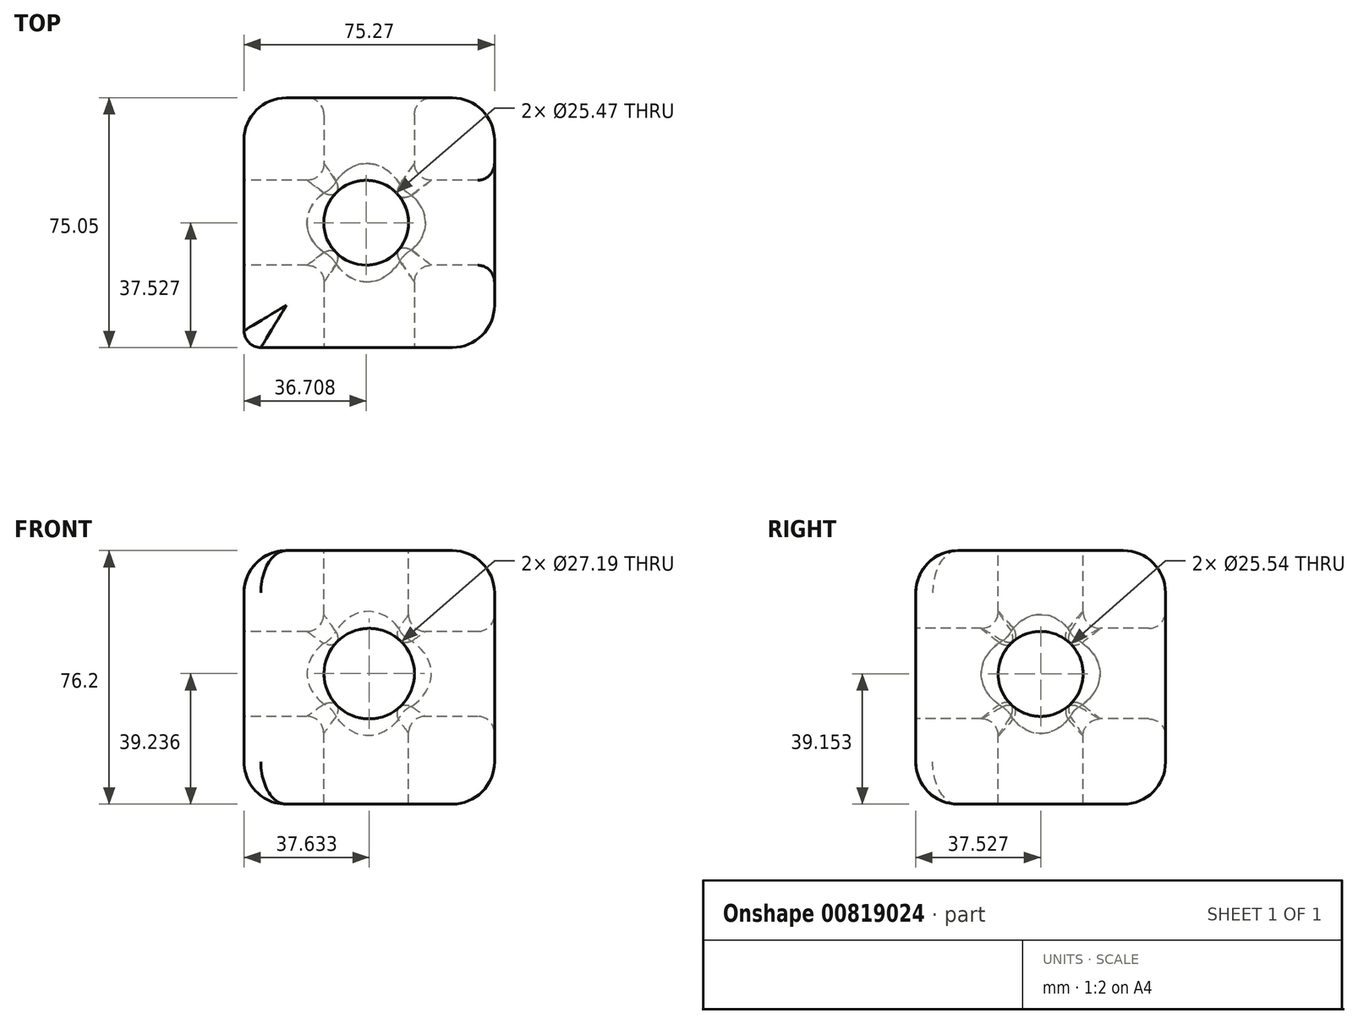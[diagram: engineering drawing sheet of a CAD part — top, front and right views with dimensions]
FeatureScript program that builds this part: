
annotation { "Feature Type Name" : "Feature", "Feature Type Description" : "" }
export const myFeature = defineFeature(function(context is Context, id is Id, definition is map)
    precondition{}
    {
        {
            var Q0;
            Q0=qCreatedBy(makeId("Top.planeOp"),FACE);
            var sketch = newSketch(context, id + "F0", { "sketchPlane" : qUnion([Q0])});
            skLineSegment(sketch, "E0.bottom", {"start": v(0, 0) * mm, "end": v(-75.27, 0) * mm});
            skLineSegment(sketch, "E0.top", {"start": v(0, -75.05) * mm, "end": v(-75.27, -75.05) * mm});
            skLineSegment(sketch, "E0.left", {"start": v(0, 0) * mm, "end": v(0, -75.05) * mm});
            skLineSegment(sketch, "E0.right", {"start": v(-75.27, 0) * mm, "end": v(-75.27, -75.05) * mm});
            skSolve(sketch);
        }
        {
            var Q0;
            Q0=makeQuery(id+"F0.imprint","IMPRINT",FACE,{"disambiguationData":[TD([[makeQuery(id+"F0.imprint","IMPRINT",EDGE,{"derivedFrom":sQuery(id+"F0.wireOp",EDGE,"E0.bottom")}),1.0]])]});
            extrude(context, id + "F1", {"entities" : qUnion([Q0]), "depth" : 76.2 * mm, "offsetDistance" : 25.4 * mm});
        }
        {
            var Q0;
            Q0=makeQuery(id+"F1.opExtrude","SWEPT_FACE",FACE,{"disambiguationData":[OSD([sQuery(id+"F0.wireOp",EDGE,"E0.top")])]});
            var sketch = newSketch(context, id + "F2", { "sketchPlane" : qUnion([Q0])});
            skCircle(sketch, "E1", {"center": v(-37.64, 39.24) * mm, "radius": 13.6 * mm});
            skPoint(sketch, "E1.centerSnap0", {"position": v(-37.64, 0) * mm});
            skSolve(sketch);
        }
        {
            var Q0;
            Q0=makeQuery(id+"F2.imprint","IMPRINT",FACE,{"disambiguationData":[TD([[makeQuery(id+"F2.imprint","IMPRINT",EDGE,{"derivedFrom":sQuery(id+"F2.wireOp",EDGE,"E1")}),1.0]])]});
            var Q1;
            Q1=sQuery(id+"F2.wireOp",EDGE,"E1");
            extrude(context, id + "F3", {"entities" : qUnion([Q0]), "operationType" : NewBodyOperationType.REMOVE, "surfaceEntities" : qUnion([Q1]), "oppositeDirection" : true, "depth" : 76.2 * mm, "offsetDistance" : 25.4 * mm});
        }
        {
            var Q0;
            Q0=makeQuery(id+"F1.opExtrude","SWEPT_FACE",FACE,{"disambiguationData":[OSD([sQuery(id+"F0.wireOp",EDGE,"E0.right")])]});
            var sketch = newSketch(context, id + "F4", { "sketchPlane" : qUnion([Q0])});
            skCircle(sketch, "E2", {"center": v(37.52, 39.15) * mm, "radius": 12.77 * mm});
            skPoint(sketch, "E2.centerSnap0", {"position": v(37.52, 0) * mm});
            skSolve(sketch);
        }
        {
            var Q0;
            Q0=makeQuery(id+"F4.imprint","IMPRINT",FACE,{"disambiguationData":[TD([[makeQuery(id+"F4.imprint","IMPRINT",EDGE,{"derivedFrom":sQuery(id+"F4.wireOp",EDGE,"E2")}),1.0]])]});
            extrude(context, id + "F5", {"entities" : qUnion([Q0]), "operationType" : NewBodyOperationType.REMOVE, "oppositeDirection" : true, "depth" : 76.2 * mm, "offsetDistance" : 25.4 * mm});
        }
        {
            var Q0;
            Q0=makeQuery(id+"F1.opExtrude","CAP_FACE",FACE,{"disambiguationData":[OSD([sQuery(id+"F0.wireOp",EDGE,"E0.bottom"),sQuery(id+"F0.wireOp",EDGE,"E0.top"),sQuery(id+"F0.wireOp",EDGE,"E0.left"),sQuery(id+"F0.wireOp",EDGE,"E0.right")])],"isStart":false});
            var sketch = newSketch(context, id + "F6", { "sketchPlane" : qUnion([Q0])});
            skCircle(sketch, "E3", {"center": v(-38.56, -37.52) * mm, "radius": 12.73 * mm});
            skPoint(sketch, "E3.centerSnap0", {"position": v(0, -37.52) * mm});
            skSolve(sketch);
        }
        {
            var Q0;
            Q0=makeQuery(id+"F6.imprint","IMPRINT",FACE,{"disambiguationData":[TD([[makeQuery(id+"F6.imprint","IMPRINT",EDGE,{"derivedFrom":sQuery(id+"F6.wireOp",EDGE,"E3")}),1.0]])]});
            var Q1;
            Q1=sQuery(id+"F6.wireOp",EDGE,"E3");
            extrude(context, id + "F7", {"entities" : qUnion([Q0]), "operationType" : NewBodyOperationType.REMOVE, "surfaceEntities" : qUnion([Q1]), "oppositeDirection" : true, "depth" : 76.2 * mm, "offsetDistance" : 25.4 * mm});
        }
        {
            var Q0;
            Q0=makeQuery(id+"F1.opExtrude","CAP_EDGE",EDGE,{"disambiguationData":[OSD([sQuery(id+"F0.wireOp",EDGE,"E0.top")])],"isStart":false});
            var Q1;
            Q1=makeQuery(id+"F1.opExtrude","CAP_EDGE",EDGE,{"disambiguationData":[OSD([sQuery(id+"F0.wireOp",EDGE,"E0.right")])],"isStart":false});
            var Q2;
            Q2=makeQuery(id+"F1.opExtrude","CAP_EDGE",EDGE,{"disambiguationData":[OSD([sQuery(id+"F0.wireOp",EDGE,"E0.bottom")])],"isStart":false});
            var Q3;
            Q3=makeQuery(id+"F1.opExtrude","CAP_EDGE",EDGE,{"disambiguationData":[OSD([sQuery(id+"F0.wireOp",EDGE,"E0.left")])],"isStart":false});
            var Q4;
            Q4=makeQuery(id+"F1.opExtrude","SWEPT_EDGE",EDGE,{"disambiguationData":[OSD([sQuery(id+"F0.wireOp",EDGE,"E0.top"),sQuery(id+"F0.wireOp",EDGE,"E0.left")])]});
            var Q5;
            Q5=makeQuery(id+"F1.opExtrude","CAP_EDGE",EDGE,{"disambiguationData":[OSD([sQuery(id+"F0.wireOp",EDGE,"E0.top")])],"isStart":true});
            var Q6;
            Q6=makeQuery(id+"F1.opExtrude","CAP_EDGE",EDGE,{"disambiguationData":[OSD([sQuery(id+"F0.wireOp",EDGE,"E0.left")])],"isStart":true});
            var Q7;
            Q7=makeQuery(id+"F1.opExtrude","CAP_EDGE",EDGE,{"disambiguationData":[OSD([sQuery(id+"F0.wireOp",EDGE,"E0.right")])],"isStart":true});
            var Q8;
            Q8=makeQuery(id+"F1.opExtrude","SWEPT_EDGE",EDGE,{"disambiguationData":[OSD([sQuery(id+"F0.wireOp",EDGE,"E0.bottom"),sQuery(id+"F0.wireOp",EDGE,"E0.right")])]});
            var Q9;
            Q9=makeQuery(id+"F1.opExtrude","CAP_EDGE",EDGE,{"disambiguationData":[OSD([sQuery(id+"F0.wireOp",EDGE,"E0.bottom")])],"isStart":true});
            var Q10;
            Q10=makeQuery(id+"F1.opExtrude","SWEPT_EDGE",EDGE,{"disambiguationData":[OSD([sQuery(id+"F0.wireOp",EDGE,"E0.bottom"),sQuery(id+"F0.wireOp",EDGE,"E0.left")])]});
            fillet(context, id + "F8", {"entities" : qUnion([Q0, Q1, Q2, Q3, Q4, Q5, Q6, Q7, Q8, Q9, Q10]), "radius" : 12.7 * mm, "tangentPropagation" : true, "allowEdgeOverflow" : false});
        }
        {
            var Q0;
            Q0=makeQuery(id+"F5.boolean.opBoolean","COPY",EDGE,{"derivedFrom":makeQuery(id+"F5.opExtrude","CAP_EDGE",EDGE,{"disambiguationData":[OSD([sQuery(id+"F4.wireOp",EDGE,"E2")])],"isStart":true})});
            var Q1;
            Q1=makeQuery(id+"F1.opExtrude","SWEPT_EDGE",EDGE,{"disambiguationData":[OSD([sQuery(id+"F0.wireOp",EDGE,"E0.top"),sQuery(id+"F0.wireOp",EDGE,"E0.right")])]});
            var Q2;
            Q2=makeQuery(id+"F3.boolean.opBoolean","COPY",EDGE,{"derivedFrom":makeQuery(id+"F3.opExtrude","CAP_EDGE",EDGE,{"disambiguationData":[OSD([sQuery(id+"F2.wireOp",EDGE,"E1")])],"isStart":true})});
            var Q3;
            Q3=makeQuery(id+"F7.boolean.opBoolean","COPY",EDGE,{"derivedFrom":makeQuery(id+"F7.opExtrude","CAP_EDGE",EDGE,{"disambiguationData":[OSD([sQuery(id+"F6.wireOp",EDGE,"E3")])],"isStart":true})});
            var Q4;
            Q4=makeQuery(id+"F5.boolean.opBoolean","INTERSECT",EDGE,{"derivedFrom":[makeQuery(id+"F1.opExtrude","SWEPT_FACE",FACE,{"disambiguationData":[OSD([sQuery(id+"F0.wireOp",EDGE,"E0.left")])]}),makeQuery(id+"F5.opExtrude","SWEPT_FACE",FACE,{"disambiguationData":[OSD([sQuery(id+"F4.wireOp",EDGE,"E2")])]})]});
            var Q5;
            Q5=makeQuery(id+"F7.boolean.opBoolean","COPY",EDGE,{"derivedFrom":makeQuery(id+"F7.opExtrude","CAP_EDGE",EDGE,{"disambiguationData":[OSD([sQuery(id+"F6.wireOp",EDGE,"E3")])],"isStart":false})});
            var Q6;
            Q6=makeQuery(id+"F3.boolean.opBoolean","INTERSECT",EDGE,{"derivedFrom":[makeQuery(id+"F1.opExtrude","SWEPT_FACE",FACE,{"disambiguationData":[OSD([sQuery(id+"F0.wireOp",EDGE,"E0.bottom")])]}),makeQuery(id+"F3.opExtrude","SWEPT_FACE",FACE,{"disambiguationData":[OSD([sQuery(id+"F2.wireOp",EDGE,"E1")])]})]});
            fillet(context, id + "F9", {"entities" : qUnion([Q0, Q1, Q2, Q3, Q4, Q5, Q6]), "radius" : 5.08 * mm, "tangentPropagation" : true, "allowEdgeOverflow" : false});
        }
        {
            var Q0;
            Q0=makeQuery(id+"F7.boolean.opBoolean","SPLIT",EDGE,{"disambiguationData":[OD(1.0)],"derivedFrom":makeQuery(id+"F5.boolean.opBoolean","INTERSECT",EDGE,{"disambiguationData":[OD(1.0)],"derivedFrom":[makeQuery(id+"F3.boolean.opBoolean","COPY",FACE,{"derivedFrom":makeQuery(id+"F3.opExtrude","SWEPT_FACE",FACE,{"disambiguationData":[OSD([sQuery(id+"F2.wireOp",EDGE,"E1")])]})}),makeQuery(id+"F5.opExtrude","SWEPT_FACE",FACE,{"disambiguationData":[OSD([sQuery(id+"F4.wireOp",EDGE,"E2")])]})]})});
            var Q1;
            Q1=makeQuery(id+"F7.boolean.opBoolean","SPLIT",EDGE,{"disambiguationData":[OD(0.0)],"derivedFrom":makeQuery(id+"F5.boolean.opBoolean","INTERSECT",EDGE,{"disambiguationData":[OD(1.0)],"derivedFrom":[makeQuery(id+"F3.boolean.opBoolean","COPY",FACE,{"derivedFrom":makeQuery(id+"F3.opExtrude","SWEPT_FACE",FACE,{"disambiguationData":[OSD([sQuery(id+"F2.wireOp",EDGE,"E1")])]})}),makeQuery(id+"F5.opExtrude","SWEPT_FACE",FACE,{"disambiguationData":[OSD([sQuery(id+"F4.wireOp",EDGE,"E2")])]})]})});
            var Q2;
            Q2=makeQuery(id+"F7.boolean.opBoolean","INTERSECT",EDGE,{"disambiguationData":[OD(1.0)],"derivedFrom":[makeQuery(id+"F5.boolean.opBoolean","COPY",FACE,{"disambiguationData":[TD([makeQuery(id+"F1.opExtrude","SWEPT_FACE",FACE,{"disambiguationData":[OSD([sQuery(id+"F0.wireOp",EDGE,"E0.left")])]})])],"derivedFrom":makeQuery(id+"F5.opExtrude","SWEPT_FACE",FACE,{"disambiguationData":[OSD([sQuery(id+"F4.wireOp",EDGE,"E2")])]})}),makeQuery(id+"F7.opExtrude","SWEPT_FACE",FACE,{"disambiguationData":[OSD([sQuery(id+"F6.wireOp",EDGE,"E3")])]})]});
            var Q3;
            Q3=makeQuery(id+"F7.boolean.opBoolean","INTERSECT",EDGE,{"disambiguationData":[OD(0.0)],"derivedFrom":[makeQuery(id+"F5.boolean.opBoolean","COPY",FACE,{"disambiguationData":[TD([makeQuery(id+"F1.opExtrude","SWEPT_FACE",FACE,{"disambiguationData":[OSD([sQuery(id+"F0.wireOp",EDGE,"E0.left")])]})])],"derivedFrom":makeQuery(id+"F5.opExtrude","SWEPT_FACE",FACE,{"disambiguationData":[OSD([sQuery(id+"F4.wireOp",EDGE,"E2")])]})}),makeQuery(id+"F7.opExtrude","SWEPT_FACE",FACE,{"disambiguationData":[OSD([sQuery(id+"F6.wireOp",EDGE,"E3")])]})]});
            var Q4;
            Q4=makeQuery(id+"F7.boolean.opBoolean","INTERSECT",EDGE,{"disambiguationData":[OD(0.0)],"derivedFrom":[makeQuery(id+"F3.boolean.opBoolean","COPY",FACE,{"derivedFrom":makeQuery(id+"F3.opExtrude","SWEPT_FACE",FACE,{"disambiguationData":[OSD([sQuery(id+"F2.wireOp",EDGE,"E1")])]})}),makeQuery(id+"F7.opExtrude","SWEPT_FACE",FACE,{"disambiguationData":[OSD([sQuery(id+"F6.wireOp",EDGE,"E3")])]})]});
            var Q5;
            Q5=makeQuery(id+"F7.boolean.opBoolean","SPLIT",EDGE,{"disambiguationData":[OD(0.0)],"derivedFrom":makeQuery(id+"F5.boolean.opBoolean","INTERSECT",EDGE,{"disambiguationData":[OD(0.0)],"derivedFrom":[makeQuery(id+"F3.boolean.opBoolean","COPY",FACE,{"derivedFrom":makeQuery(id+"F3.opExtrude","SWEPT_FACE",FACE,{"disambiguationData":[OSD([sQuery(id+"F2.wireOp",EDGE,"E1")])]})}),makeQuery(id+"F5.opExtrude","SWEPT_FACE",FACE,{"disambiguationData":[OSD([sQuery(id+"F4.wireOp",EDGE,"E2")])]})]})});
            var Q6;
            Q6=makeQuery(id+"F7.boolean.opBoolean","INTERSECT",EDGE,{"disambiguationData":[OD(0.0)],"derivedFrom":[makeQuery(id+"F5.boolean.opBoolean","COPY",FACE,{"disambiguationData":[TD([makeQuery(id+"F1.opExtrude","SWEPT_FACE",FACE,{"disambiguationData":[OSD([sQuery(id+"F0.wireOp",EDGE,"E0.right")])]})])],"derivedFrom":makeQuery(id+"F5.opExtrude","SWEPT_FACE",FACE,{"disambiguationData":[OSD([sQuery(id+"F4.wireOp",EDGE,"E2")])]})}),makeQuery(id+"F7.opExtrude","SWEPT_FACE",FACE,{"disambiguationData":[OSD([sQuery(id+"F6.wireOp",EDGE,"E3")])]})]});
            var Q7;
            Q7=makeQuery(id+"F7.boolean.opBoolean","INTERSECT",EDGE,{"disambiguationData":[OD(3.0)],"derivedFrom":[makeQuery(id+"F3.boolean.opBoolean","COPY",FACE,{"derivedFrom":makeQuery(id+"F3.opExtrude","SWEPT_FACE",FACE,{"disambiguationData":[OSD([sQuery(id+"F2.wireOp",EDGE,"E1")])]})}),makeQuery(id+"F7.opExtrude","SWEPT_FACE",FACE,{"disambiguationData":[OSD([sQuery(id+"F6.wireOp",EDGE,"E3")])]})]});
            var Q8;
            Q8=makeQuery(id+"F7.boolean.opBoolean","SPLIT",EDGE,{"disambiguationData":[OD(1.0)],"derivedFrom":makeQuery(id+"F5.boolean.opBoolean","INTERSECT",EDGE,{"disambiguationData":[OD(0.0)],"derivedFrom":[makeQuery(id+"F3.boolean.opBoolean","COPY",FACE,{"derivedFrom":makeQuery(id+"F3.opExtrude","SWEPT_FACE",FACE,{"disambiguationData":[OSD([sQuery(id+"F2.wireOp",EDGE,"E1")])]})}),makeQuery(id+"F5.opExtrude","SWEPT_FACE",FACE,{"disambiguationData":[OSD([sQuery(id+"F4.wireOp",EDGE,"E2")])]})]})});
            var Q9;
            Q9=makeQuery(id+"F7.boolean.opBoolean","INTERSECT",EDGE,{"disambiguationData":[OD(1.0)],"derivedFrom":[makeQuery(id+"F5.boolean.opBoolean","COPY",FACE,{"disambiguationData":[TD([makeQuery(id+"F1.opExtrude","SWEPT_FACE",FACE,{"disambiguationData":[OSD([sQuery(id+"F0.wireOp",EDGE,"E0.right")])]})])],"derivedFrom":makeQuery(id+"F5.opExtrude","SWEPT_FACE",FACE,{"disambiguationData":[OSD([sQuery(id+"F4.wireOp",EDGE,"E2")])]})}),makeQuery(id+"F7.opExtrude","SWEPT_FACE",FACE,{"disambiguationData":[OSD([sQuery(id+"F6.wireOp",EDGE,"E3")])]})]});
            var Q10;
            Q10=makeQuery(id+"F7.boolean.opBoolean","INTERSECT",EDGE,{"disambiguationData":[OD(2.0)],"derivedFrom":[makeQuery(id+"F3.boolean.opBoolean","COPY",FACE,{"derivedFrom":makeQuery(id+"F3.opExtrude","SWEPT_FACE",FACE,{"disambiguationData":[OSD([sQuery(id+"F2.wireOp",EDGE,"E1")])]})}),makeQuery(id+"F7.opExtrude","SWEPT_FACE",FACE,{"disambiguationData":[OSD([sQuery(id+"F6.wireOp",EDGE,"E3")])]})]});
            var Q11;
            Q11=makeQuery(id+"F7.boolean.opBoolean","INTERSECT",EDGE,{"disambiguationData":[OD(1.0)],"derivedFrom":[makeQuery(id+"F3.boolean.opBoolean","COPY",FACE,{"derivedFrom":makeQuery(id+"F3.opExtrude","SWEPT_FACE",FACE,{"disambiguationData":[OSD([sQuery(id+"F2.wireOp",EDGE,"E1")])]})}),makeQuery(id+"F7.opExtrude","SWEPT_FACE",FACE,{"disambiguationData":[OSD([sQuery(id+"F6.wireOp",EDGE,"E3")])]})]});
            fillet(context, id + "F10", {"entities" : qUnion([Q0, Q1, Q2, Q3, Q4, Q5, Q6, Q7, Q8, Q9, Q10, Q11]), "radius" : 5.08 * mm, "tangentPropagation" : true, "allowEdgeOverflow" : false});
        }
    });
